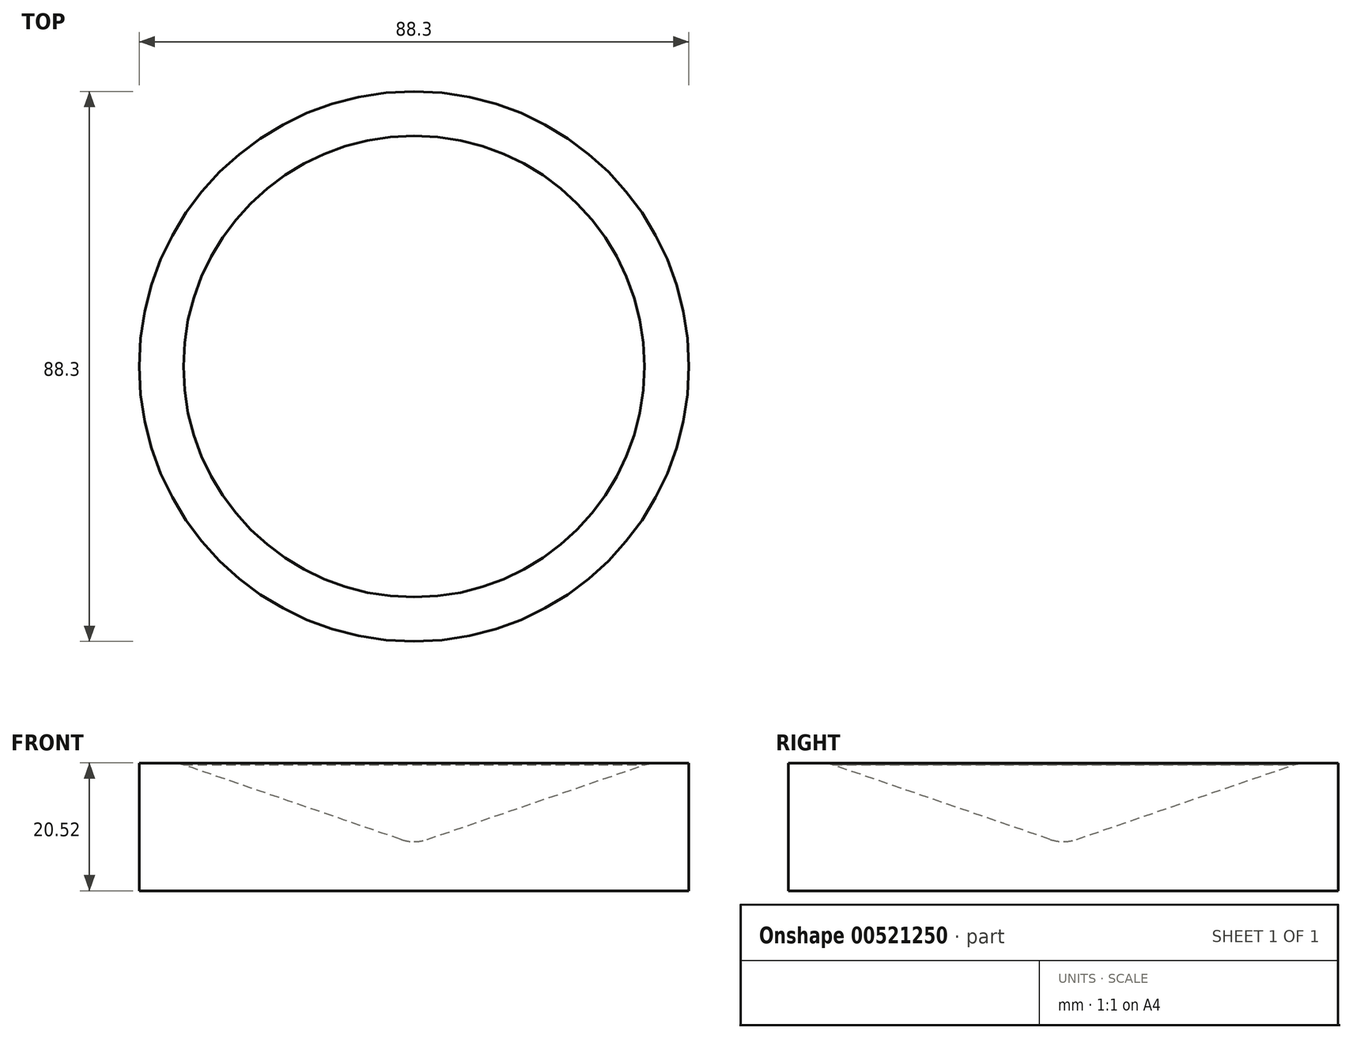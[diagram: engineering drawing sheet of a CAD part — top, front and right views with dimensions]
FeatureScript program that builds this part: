
annotation { "Feature Type Name" : "Feature", "Feature Type Description" : "" }
export const myFeature = defineFeature(function(context is Context, id is Id, definition is map)
    precondition{}
    {
        {
            var Q0;
            Q0=qCreatedBy(makeId("Front.planeOp"),FACE);
            var sketch = newSketch(context, id + "F0", { "sketchPlane" : qUnion([Q0])});
            skLineSegment(sketch, "E0", {"start": v(-44.15, 0) * mm, "end": v(0, 0) * mm});
            skLineSegment(sketch, "E1", {"start": v(0, 0) * mm, "end": v(0, 7.88) * mm});
            skLineSegment(sketch, "E2", {"start": v(-44.15, 20.52) * mm, "end": v(-44.15, 0) * mm});
            skLineSegment(sketch, "E3", {"start": v(-44.15, 20.52) * mm, "end": v(-38.98, 20.52) * mm});
            skPoint(sketch, "E4.visualSharp", {"position": v(-37.99, 20.52) * mm});
            skArc(sketch, "E4.filletArc", {"start": v(-37.04, 20.21) * mm, "mid": v(-38, 20.44) * mm, "end": v(-38.98, 20.52) * mm});
            skLineSegment(sketch, "E5", {"start": v(-37.04, 20.21) * mm, "end": v(-2.1, 8.23) * mm});
            skArc(sketch, "E6", {"start": v(-2.1, 8.23) * mm, "mid": v(-1.06, 7.97) * mm, "end": v(0, 7.88) * mm});
            skSolve(sketch);
        }
        {
            var Q0;
            Q0 = qSketchRegion(id + "F0", true);
            var Q1;
            Q1=sQuery(id+"F0.wireOp",EDGE,"E1");
            revolve(context, id + "F1", {"entities" : qUnion([Q0]), "axis" : qUnion([Q1]), "revolveType" : RevolveType.FULL});
        }
    });
